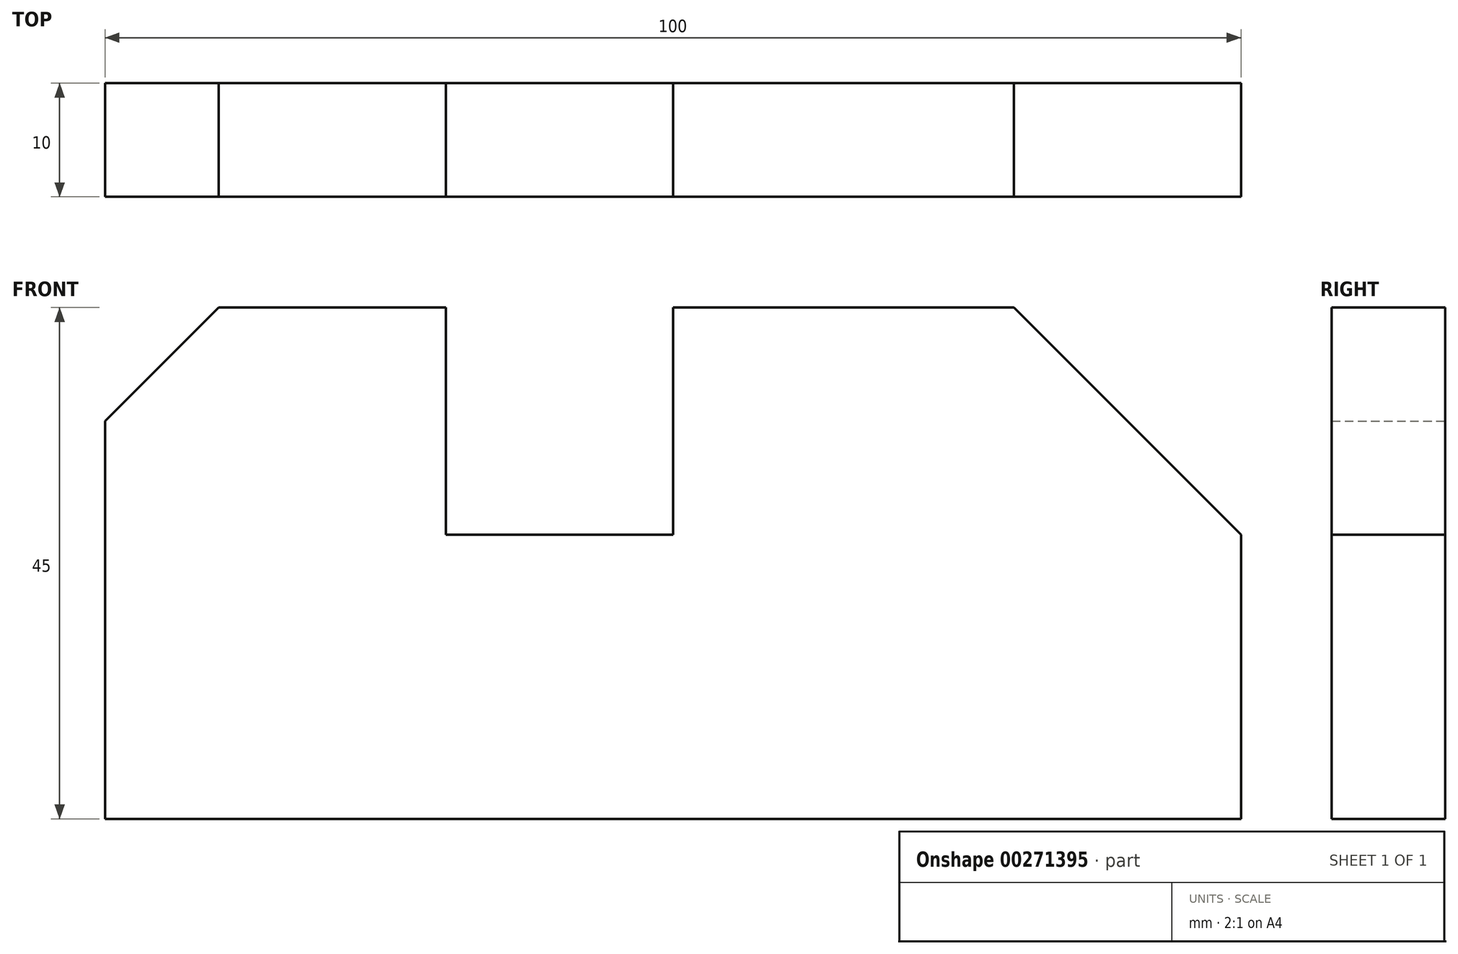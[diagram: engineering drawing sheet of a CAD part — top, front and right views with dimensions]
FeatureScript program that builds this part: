
annotation { "Feature Type Name" : "Feature", "Feature Type Description" : "" }
export const myFeature = defineFeature(function(context is Context, id is Id, definition is map)
    precondition{}
    {
        {
            var Q0;
            Q0=qCreatedBy(makeId("Front.planeOp"),FACE);
            var sketch = newSketch(context, id + "F0", { "sketchPlane" : qUnion([Q0])});
            skLineSegment(sketch, "E0", {"start": v(0, 0) * mm, "end": v(100, 0) * mm});
            skLineSegment(sketch, "E1", {"start": v(100, 0) * mm, "end": v(100, 25) * mm});
            skLineSegment(sketch, "E2", {"start": v(100, 25) * mm, "end": v(80, 45) * mm});
            skLineSegment(sketch, "E3", {"start": v(80, 45) * mm, "end": v(50, 45) * mm});
            skLineSegment(sketch, "E4", {"start": v(50, 45) * mm, "end": v(50, 25) * mm});
            skLineSegment(sketch, "E5", {"start": v(50, 25) * mm, "end": v(30, 25) * mm});
            skLineSegment(sketch, "E6", {"start": v(30, 25) * mm, "end": v(30, 45) * mm});
            skLineSegment(sketch, "E7", {"start": v(30, 45) * mm, "end": v(10, 45) * mm});
            skLineSegment(sketch, "E8", {"start": v(10, 45) * mm, "end": v(0, 35) * mm});
            skLineSegment(sketch, "E9", {"start": v(0, 35) * mm, "end": v(0, 0) * mm});
            skSolve(sketch);
        }
        {
            var Q0;
            Q0 = qSketchRegion(id + "F0", true);
            extrude(context, id + "F1", {"entities" : qUnion([Q0]), "depth" : 10 * mm});
        }
    });
